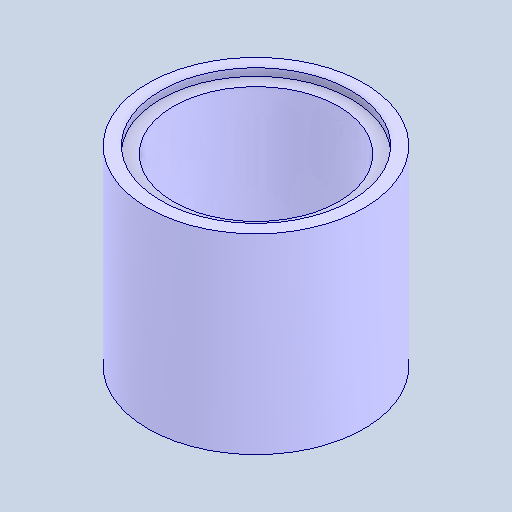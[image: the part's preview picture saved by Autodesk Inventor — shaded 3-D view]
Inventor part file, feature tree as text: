
AUTODESK INVENTOR PART (.ipt)
format: ipt  version: 2024.1 (Build 281209000, 209)  size: 115,200 bytes
history: native  units: in
note: dims shown in document units (in); Inventor stores cm internally (conversion verified against a paired STEP export)
features: chamfer x1
ambient origin geometry x8: Origin, YZ Plane, XZ Plane, XY Plane, X Axis, Y Axis, Z Axis, Center Point
bodies: Solid1 (feature_tree)
feature tree (1):
  chamfer  "Chamfer1"  [1 undecoded]
note: 1 required parameter value undecoded (feature->parameter linkage not recoverable at this tier; creation-order binding heuristic only, values carry confidence <= 0.55)
